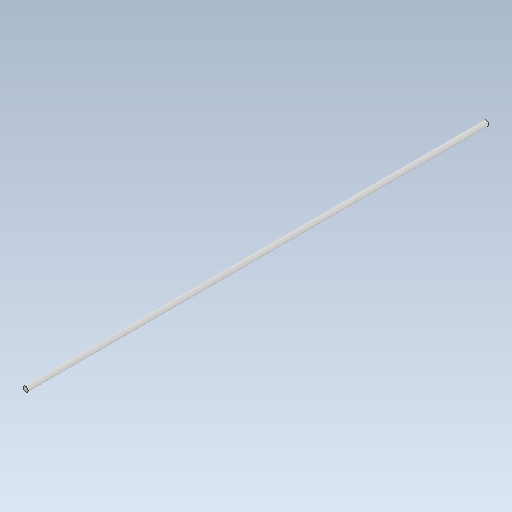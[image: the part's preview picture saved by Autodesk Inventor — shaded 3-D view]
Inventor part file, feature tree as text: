
AUTODESK INVENTOR PART (.ipt)
format: ipt  version: 2020 (Build 240168000, 168)  size: 90,112 bytes
history: native  units: mm
features: other x5, extrude x1, sketch x1
ambient origin geometry x8: Origin, YZ Plane, XZ Plane, XY Plane, X Axis, Y Axis, Z Axis, Center Point
bodies: Body1 (feature_tree)
feature tree (7):
  other  "Sólido1"
  extrude  "Extrusão1"  [1 undecoded]
  sketch  "Esboço1"  dims[d0=144.0mm d1=0.0mm]
  other  "Referência1"
  other  "<userpath>\Desktop\rabo\3d\ela.iam"
  other  "ela.iam"
  other  "microservoSG90:1"
note: 1 required parameter value undecoded (feature->parameter linkage not recoverable at this tier; creation-order binding heuristic only, values carry confidence <= 0.55)
